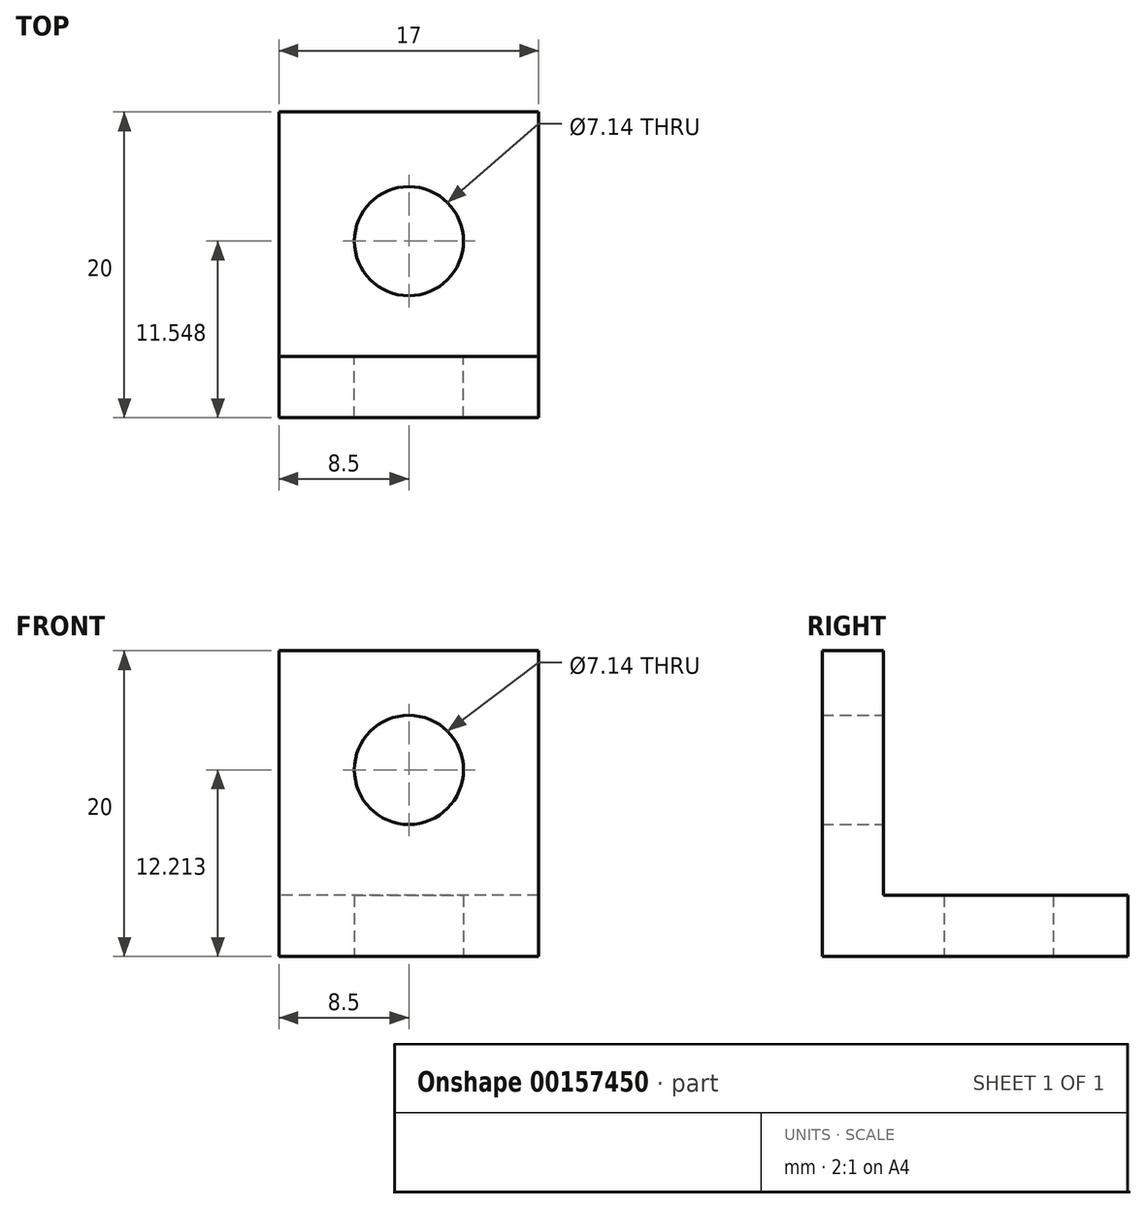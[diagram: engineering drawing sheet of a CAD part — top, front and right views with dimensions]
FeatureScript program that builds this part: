
annotation { "Feature Type Name" : "Feature", "Feature Type Description" : "" }
export const myFeature = defineFeature(function(context is Context, id is Id, definition is map)
    precondition{}
    {
        {
            var Q0;
            Q0=qCreatedBy(makeId("Front.planeOp"),FACE);
            var sketch = newSketch(context, id + "F0", { "sketchPlane" : qUnion([Q0])});
            skLineSegment(sketch, "E0.bottom", {"start": v(8.5, -10) * mm, "end": v(-8.5, -10) * mm});
            skLineSegment(sketch, "E0.top", {"start": v(8.5, 10) * mm, "end": v(-8.5, 10) * mm});
            skLineSegment(sketch, "E0.left", {"start": v(8.5, -10) * mm, "end": v(8.5, 10) * mm});
            skLineSegment(sketch, "E0.right", {"start": v(-8.5, -10) * mm, "end": v(-8.5, 10) * mm});
            skPoint(sketch, "E0.middle", {"position": v(0, 0) * mm});
            skCircle(sketch, "E1", {"center": v(0, 2.21) * mm, "radius": 3.57 * mm});
            skSolve(sketch);
        }
        {
            var Q0;
            Q0=makeQuery(id+"F0.imprint","IMPRINT",FACE,{"disambiguationData":[TD([[makeQuery(id+"F0.imprint","IMPRINT",EDGE,{"derivedFrom":sQuery(id+"F0.wireOp",EDGE,"E0.bottom")}),-1.0]])]});
            extrude(context, id + "F1", {"entities" : qUnion([Q0]), "depth" : 4 * mm});
        }
        {
            var Q0;
            Q0=makeQuery(id+"F1.opExtrude","SWEPT_FACE",FACE,{"disambiguationData":[OSD([sQuery(id+"F0.wireOp",EDGE,"E0.bottom")])]});
            var sketch = newSketch(context, id + "F2", { "sketchPlane" : qUnion([Q0])});
            skLineSegment(sketch, "E2.bottom", {"start": v(-8.5, 4) * mm, "end": v(8.5, 4) * mm});
            skLineSegment(sketch, "E2.top", {"start": v(-8.5, -16) * mm, "end": v(8.5, -16) * mm});
            skLineSegment(sketch, "E2.left", {"start": v(-8.5, 4) * mm, "end": v(-8.5, -16) * mm});
            skLineSegment(sketch, "E2.right", {"start": v(8.5, 4) * mm, "end": v(8.5, -16) * mm});
            skCircle(sketch, "E3", {"center": v(0, -7.55) * mm, "radius": 3.57 * mm});
            skSolve(sketch);
        }
        {
            var Q0;
            {var subQ2=sQuery(id+"F2.wireOp",EDGE,"E2.top");Q0=makeQuery(id+"F2.imprint","IMPRINT",FACE,{"disambiguationData":[TD([[makeQuery(id+"F2.imprint","IMPRINT",EDGE,{"derivedFrom":subQ2}),1.0]])]});}
            extrude(context, id + "F3", {"entities" : qUnion([Q0]), "operationType" : NewBodyOperationType.ADD, "oppositeDirection" : true, "depth" : 4 * mm});
        }
    });
